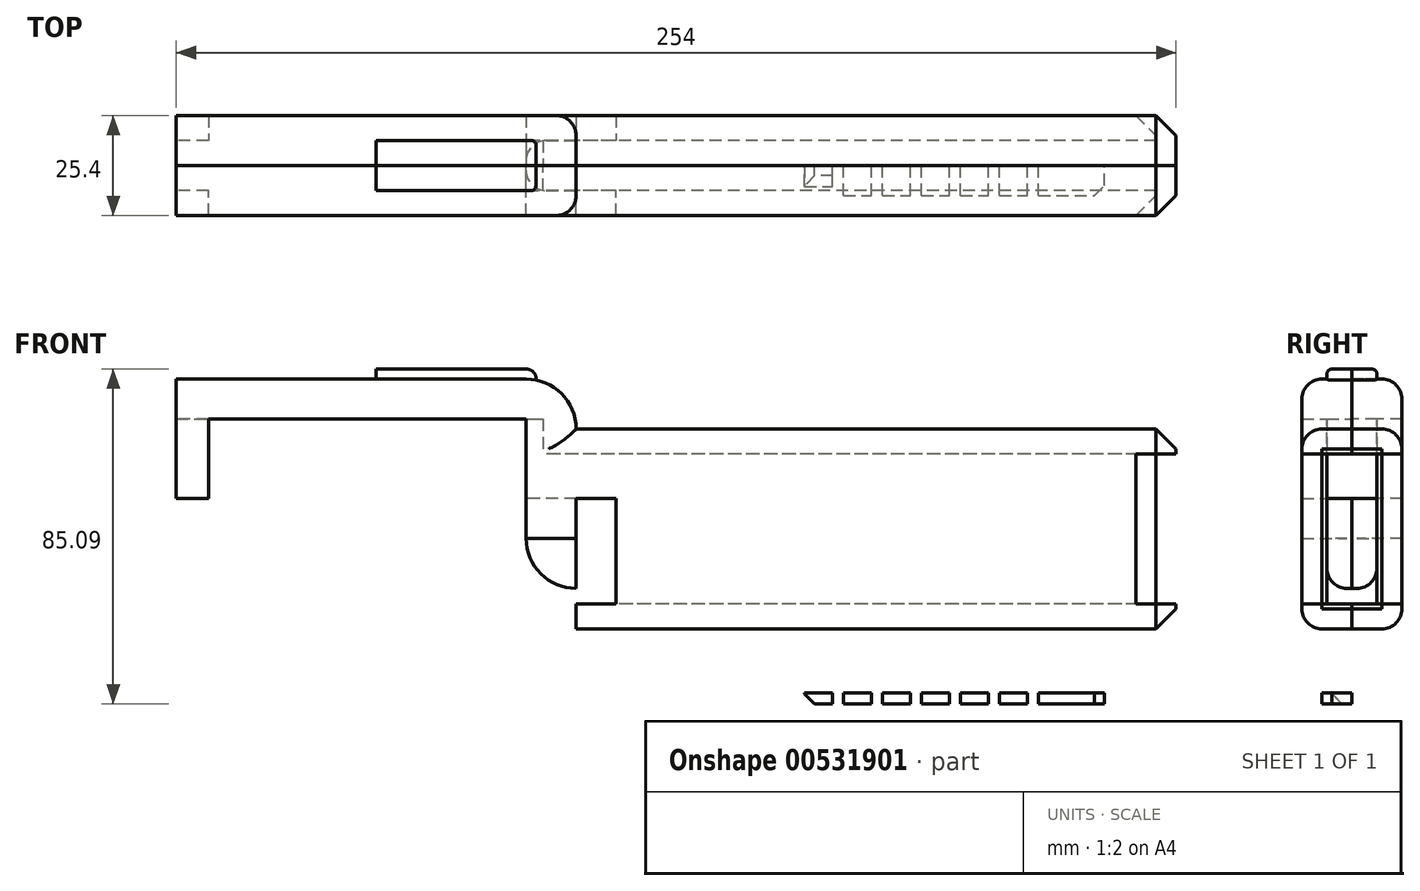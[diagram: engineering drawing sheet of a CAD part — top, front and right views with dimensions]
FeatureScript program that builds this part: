
annotation { "Feature Type Name" : "Feature", "Feature Type Description" : "" }
export const myFeature = defineFeature(function(context is Context, id is Id, definition is map)
    precondition{}
    {
        {
            var Q0;
            Q0=qCreatedBy(makeId("Front.planeOp"),FACE);
            var sketch = newSketch(context, id + "F0", { "sketchPlane" : qUnion([Q0])});
            skLineSegment(sketch, "E0.bottom", {"start": v(-50.8, 20.24) * mm, "end": v(38.1, 20.24) * mm});
            skLineSegment(sketch, "E0.top", {"start": v(-50.8, -20.24) * mm, "end": v(50.8, -20.24) * mm});
            skLineSegment(sketch, "E0.left", {"start": v(-50.8, 20.24) * mm, "end": v(-50.8, -20.24) * mm});
            skLineSegment(sketch, "E0.right", {"start": v(50.8, 7.54) * mm, "end": v(50.8, -20.24) * mm});
            skPoint(sketch, "E0.middle", {"position": v(0, 0) * mm});
            skPoint(sketch, "E1.visualSharp", {"position": v(50.8, 20.24) * mm});
            skArc(sketch, "E1.filletArc", {"start": v(50.8, 7.54) * mm, "mid": v(47.08, 16.52) * mm, "end": v(38.1, 20.24) * mm});
            skPoint(sketch, "E2", {"position": v(0, 20.24) * mm});
            skLineSegment(sketch, "E3", {"start": v(0, 20.24) * mm, "end": v(0, 22.78) * mm});
            skLineSegment(sketch, "E4", {"start": v(0, 22.78) * mm, "end": v(38.1, 22.78) * mm});
            skLineSegment(sketch, "E5", {"start": v(38.1, 22.78) * mm, "end": v(38.1, 20.24) * mm});
            skArc(sketch, "E6", {"start": v(38.1, 22.78) * mm, "mid": v(39.98, 21.95) * mm, "end": v(40.63, 19.99) * mm});
            skLineSegment(sketch, "E7.bottom", {"start": v(50.8, 7.54) * mm, "end": v(203.2, 7.54) * mm});
            skLineSegment(sketch, "E7.top", {"start": v(50.8, -43.26) * mm, "end": v(203.2, -43.26) * mm});
            skLineSegment(sketch, "E7.left", {"start": v(50.8, 7.54) * mm, "end": v(50.8, -43.26) * mm});
            skLineSegment(sketch, "E7.right", {"start": v(203.2, 7.54) * mm, "end": v(203.2, -43.26) * mm});
            skLineSegment(sketch, "E8", {"start": v(38.1, 20.24) * mm, "end": v(38.1, -20.24) * mm});
            skArc(sketch, "E9", {"start": v(38.1, -20.24) * mm, "mid": v(41.82, -29.22) * mm, "end": v(50.8, -32.94) * mm});
            skLineSegment(sketch, "E10.bottom", {"start": v(203.2, 1.2) * mm, "end": v(198.12, 1.2) * mm});
            skLineSegment(sketch, "E10.top", {"start": v(203.2, -36.9) * mm, "end": v(198.12, -36.9) * mm});
            skLineSegment(sketch, "E10.left", {"start": v(203.2, 1.2) * mm, "end": v(203.2, -36.9) * mm});
            skLineSegment(sketch, "E10.right", {"start": v(198.12, 1.2) * mm, "end": v(198.12, -36.9) * mm});
            skLineSegment(sketch, "E11", {"start": v(198.12, 1.2) * mm, "end": v(50.8, 1.2) * mm});
            skLineSegment(sketch, "E12", {"start": v(198.12, -36.9) * mm, "end": v(50.8, -36.9) * mm});
            skLineSegment(sketch, "E13", {"start": v(60.96, 1.2) * mm, "end": v(60.96, -36.9) * mm});
            skLineSegment(sketch, "E14", {"start": v(60.96, -10.08) * mm, "end": v(-42.63, -10.08) * mm});
            skLineSegment(sketch, "E15", {"start": v(-42.63, -10.08) * mm, "end": v(-42.63, 10.08) * mm});
            skLineSegment(sketch, "E16", {"start": v(-42.63, 10.08) * mm, "end": v(42.45, 10.08) * mm});
            skLineSegment(sketch, "E17", {"start": v(42.45, 10.08) * mm, "end": v(42.45, 1.2) * mm});
            skLineSegment(sketch, "E18", {"start": v(42.45, 1.2) * mm, "end": v(50.8, 1.2) * mm});
            skLineSegment(sketch, "E19.bottom", {"start": v(-42.63, 10.08) * mm, "end": v(-50.8, 10.08) * mm});
            skLineSegment(sketch, "E19.top", {"start": v(-42.63, -10.08) * mm, "end": v(-50.8, -10.08) * mm});
            skLineSegment(sketch, "E19.left", {"start": v(-42.63, 10.08) * mm, "end": v(-42.63, -10.08) * mm});
            skLineSegment(sketch, "E19.right", {"start": v(-50.8, 10.08) * mm, "end": v(-50.8, -10.08) * mm});
            skLineSegment(sketch, "E20.bottom", {"start": v(108.84, -43.26) * mm, "end": v(185.04, -43.26) * mm});
            skLineSegment(sketch, "E20.top", {"start": v(108.84, -62.3) * mm, "end": v(185.04, -62.3) * mm});
            skLineSegment(sketch, "E20.left", {"start": v(108.84, -43.26) * mm, "end": v(108.84, -62.3) * mm});
            skLineSegment(sketch, "E20.right", {"start": v(185.04, -43.26) * mm, "end": v(185.04, -62.3) * mm});
            skLineSegment(sketch, "E21", {"start": v(108.84, -59.55) * mm, "end": v(185.04, -59.55) * mm});
            skLineSegment(sketch, "E22", {"start": v(115.95, -59.55) * mm, "end": v(115.95, -62.3) * mm});
            skLineSegment(sketch, "E23", {"start": v(118.74, -59.55) * mm, "end": v(118.74, -62.3) * mm});
            skLineSegment(sketch, "E24", {"start": v(125.85, -59.55) * mm, "end": v(125.85, -62.3) * mm});
            skLineSegment(sketch, "E25", {"start": v(128.65, -59.55) * mm, "end": v(128.65, -62.3) * mm});
            skLineSegment(sketch, "E26", {"start": v(135.76, -59.55) * mm, "end": v(135.76, -62.3) * mm});
            skLineSegment(sketch, "E27", {"start": v(138.55, -59.55) * mm, "end": v(138.55, -62.3) * mm});
            skLineSegment(sketch, "E28", {"start": v(145.67, -59.55) * mm, "end": v(145.67, -62.3) * mm});
            skLineSegment(sketch, "E29", {"start": v(148.46, -59.55) * mm, "end": v(148.46, -62.3) * mm});
            skLineSegment(sketch, "E30", {"start": v(155.57, -59.55) * mm, "end": v(155.57, -62.3) * mm});
            skLineSegment(sketch, "E31", {"start": v(158.37, -59.55) * mm, "end": v(158.37, -62.3) * mm});
            skLineSegment(sketch, "E32", {"start": v(165.48, -59.55) * mm, "end": v(165.48, -62.3) * mm});
            skLineSegment(sketch, "E33", {"start": v(168.27, -59.55) * mm, "end": v(168.27, -62.3) * mm});
            skSolve(sketch);
        }
        {
            var Q0;
            {var subQ0=sQuery(id+"F0.wireOp",EDGE,"E0.left");Q0=makeQuery(id+"F0.imprint","IMPRINT",FACE,{"disambiguationData":[TD([[makeQuery(id+"F0.imprint","IMPRINT",EDGE,{"derivedFrom":subQ0}),1.0]])]});}
            var Q1;
            {var subQ0=sQuery(id+"F0.wireOp",EDGE,"E8");Q1=makeQuery(id+"F0.imprint","IMPRINT",FACE,{"disambiguationData":[TD([[makeQuery(id+"F0.imprint","IMPRINT",EDGE,{"derivedFrom":subQ0}),1.0]])]});}
            var Q2;
            {var subQ3=sQuery(id+"F0.wireOp",EDGE,"E7.bottom");Q2=makeQuery(id+"F0.imprint","IMPRINT",FACE,{"disambiguationData":[TD([[makeQuery(id+"F0.imprint","IMPRINT",EDGE,{"derivedFrom":subQ3}),-1.0]])]});}
            var Q3;
            {var subQ8=sQuery(id+"F0.wireOp",EDGE,"E19.bottom");Q3=makeQuery(id+"F0.imprint","IMPRINT",FACE,{"disambiguationData":[TD([[makeQuery(id+"F0.imprint","IMPRINT",EDGE,{"derivedFrom":subQ8}),-1.0]])]});}
            var Q4;
            {var subQ9=sQuery(id+"F0.wireOp",EDGE,"E17");Q4=makeQuery(id+"F0.imprint","IMPRINT",FACE,{"disambiguationData":[TD([[makeQuery(id+"F0.imprint","IMPRINT",EDGE,{"derivedFrom":subQ9}),1.0]])]});}
            var Q5;
            Q5=makeQuery(id+"F0.imprint","IMPRINT",FACE,{"disambiguationData":[TD([[makeQuery(id+"F0.imprint","IMPRINT",EDGE,{"derivedFrom":sQuery(id+"F0.wireOp",EDGE,"E19.bottom")}),1.0]])]});
            var Q6;
            {var subQ5=sQuery(id+"F0.wireOp",EDGE,"E19.left");Q6=makeQuery(id+"F0.imprint","IMPRINT",FACE,{"disambiguationData":[TD([[makeQuery(id+"F0.imprint","IMPRINT",EDGE,{"derivedFrom":subQ5}),1.0]])]});}
            var Q7;
            {var subQ8=sQuery(id+"F0.wireOp",EDGE,"E17");Q7=makeQuery(id+"F0.imprint","IMPRINT",FACE,{"disambiguationData":[TD([[makeQuery(id+"F0.imprint","IMPRINT",EDGE,{"derivedFrom":subQ8}),-1.0]])]});}
            var Q8;
            {var subQ0=sQuery(id+"F0.wireOp",EDGE,"E11");var subQ5=sQuery(id+"F0.wireOp",EDGE,"E13");var subQ6=makeQuery(id+"F0.imprint","INTERSECT",VERTEX,{"derivedFrom":[subQ0,subQ5]});Q8=makeQuery(id+"F0.imprint","IMPRINT",FACE,{"disambiguationData":[TD([[makeQuery(id+"F0.imprint","IMPRINT",EDGE,{"disambiguationData":[TD([[subQ6,-1.0]])],"derivedFrom":subQ5}),-1.0]])]});}
            var Q9;
            {var subQ1=sQuery(id+"F0.wireOp",EDGE,"E7.left");var subQ6=makeQuery(id+"F0.imprint","INTERSECT",VERTEX,{"derivedFrom":[sQuery(id+"F0.wireOp",EDGE,"E0.top"),subQ1]});Q9=makeQuery(id+"F0.imprint","IMPRINT",FACE,{"disambiguationData":[TD([[makeQuery(id+"F0.imprint","IMPRINT",EDGE,{"disambiguationData":[TD([[subQ6,1.0]])],"derivedFrom":subQ1}),1.0]])]});}
            var Q10;
            {var subQ1=sQuery(id+"F0.wireOp",EDGE,"E10.right");Q10=makeQuery(id+"F0.imprint","IMPRINT",FACE,{"disambiguationData":[TD([[makeQuery(id+"F0.imprint","IMPRINT",EDGE,{"derivedFrom":subQ1}),-1.0]])]});}
            var Q11;
            {var subQ2=sQuery(id+"F0.wireOp",EDGE,"E7.top");Q11=makeQuery(id+"F0.imprint","IMPRINT",FACE,{"disambiguationData":[TD([[makeQuery(id+"F0.imprint","IMPRINT",EDGE,{"derivedFrom":subQ2}),1.0]])]});}
            extrude(context, id + "F1", {"entities" : qUnion([Q0, Q1, Q2, Q3, Q4, Q5, Q6, Q7, Q8, Q9, Q10, Q11]), "depth" : 12.7 * mm, "offsetDistance" : 25.4 * mm});
        }
        {
            var Q0;
            {var subQ2=sQuery(id+"F0.wireOp",EDGE,"E3");Q0=makeQuery(id+"F0.imprint","IMPRINT",FACE,{"disambiguationData":[TD([[makeQuery(id+"F0.imprint","IMPRINT",EDGE,{"derivedFrom":subQ2}),-1.0]])]});}
            var Q1;
            {var subQ0=sQuery(id+"F0.wireOp",EDGE,"E5");Q1=makeQuery(id+"F0.imprint","IMPRINT",FACE,{"disambiguationData":[TD([[makeQuery(id+"F0.imprint","IMPRINT",EDGE,{"derivedFrom":subQ0}),1.0]])]});}
            var Q2;
            {var subQ3=sQuery(id+"F0.wireOp",EDGE,"E9");Q2=makeQuery(id+"F0.imprint","IMPRINT",FACE,{"disambiguationData":[TD([[makeQuery(id+"F0.imprint","IMPRINT",EDGE,{"derivedFrom":subQ3}),1.0]])]});}
            extrude(context, id + "F2", {"entities" : qUnion([Q0, Q1, Q2]), "operationType" : NewBodyOperationType.ADD, "depth" : 6.35 * mm, "offsetDistance" : 25.4 * mm});
        }
        {
            var Q0;
            Q0=makeQuery(id+"F1.opExtrude","CAP_EDGE",EDGE,{"disambiguationData":[OSD([sQuery(id+"F0.wireOp",EDGE,"E0.bottom")])],"isStart":false});
            var Q1;
            Q1=makeQuery(id+"F1.opExtrude","CAP_EDGE",EDGE,{"disambiguationData":[OSD([sQuery(id+"F0.wireOp",EDGE,"E7.bottom")])],"isStart":false});
            var Q2;
            Q2=makeQuery(id+"F2.opExtrude","CAP_EDGE",EDGE,{"disambiguationData":[OSD([sQuery(id+"F0.wireOp",EDGE,"E9")])],"isStart":false});
            var Q3;
            Q3=makeQuery(id+"F1.opExtrude","CAP_EDGE",EDGE,{"disambiguationData":[OSD([sQuery(id+"F0.wireOp",EDGE,"E7.top")])],"isStart":false});
            fillet(context, id + "F3", {"entities" : qUnion([Q0, Q1, Q2, Q3]), "radius" : 5.08 * mm, "tangentPropagation" : true, "allowEdgeOverflow" : false});
        }
        {
            var Q0;
            Q0=makeQuery(id+"F1.opExtrude","CAP_EDGE",EDGE,{"disambiguationData":[OSD([sQuery(id+"F0.wireOp",EDGE,"E7.right")])],"isStart":false});
            var Q1;
            Q1=makeQuery(id+"F1.opExtrude","CAP_EDGE",EDGE,{"disambiguationData":[OSD([sQuery(id+"F0.wireOp",EDGE,"E10.right")])],"isStart":false});
            chamfer(context, id + "F4", {"entities" : qUnion([Q0, Q1]), "width" : 5.08 * mm, "tangentPropagation" : true});
        }
        {
            var Q0;
            Q0=makeQuery(id+"F2.opExtrude","CAP_EDGE",EDGE,{"disambiguationData":[OSD([sQuery(id+"F0.wireOp",EDGE,"E4")])],"isStart":false});
            fillet(context, id + "F5", {"entities" : qUnion([Q0]), "radius" : 1.27 * mm, "tangentPropagation" : true, "allowEdgeOverflow" : false});
        }
        {
            var Q0;
            {var subQ1=sQuery(id+"F0.wireOp",EDGE,"E10.right");Q0=makeQuery(id+"F0.imprint","IMPRINT",FACE,{"disambiguationData":[TD([[makeQuery(id+"F0.imprint","IMPRINT",EDGE,{"derivedFrom":subQ1}),-1.0]])]});}
            var Q1;
            {var subQ0=sQuery(id+"F0.wireOp",EDGE,"E11");var subQ5=sQuery(id+"F0.wireOp",EDGE,"E13");var subQ6=makeQuery(id+"F0.imprint","INTERSECT",VERTEX,{"derivedFrom":[subQ0,subQ5]});Q1=makeQuery(id+"F0.imprint","IMPRINT",FACE,{"disambiguationData":[TD([[makeQuery(id+"F0.imprint","IMPRINT",EDGE,{"disambiguationData":[TD([[subQ6,-1.0]])],"derivedFrom":subQ5}),-1.0]])]});}
            var Q2;
            {var subQ5=sQuery(id+"F0.wireOp",EDGE,"E19.left");Q2=makeQuery(id+"F0.imprint","IMPRINT",FACE,{"disambiguationData":[TD([[makeQuery(id+"F0.imprint","IMPRINT",EDGE,{"derivedFrom":subQ5}),1.0]])]});}
            var Q3;
            Q3=makeQuery(id+"F0.imprint","IMPRINT",FACE,{"disambiguationData":[TD([[makeQuery(id+"F0.imprint","IMPRINT",EDGE,{"derivedFrom":sQuery(id+"F0.wireOp",EDGE,"E19.bottom")}),1.0]])]});
            var Q4;
            {var subQ8=sQuery(id+"F0.wireOp",EDGE,"E17");Q4=makeQuery(id+"F0.imprint","IMPRINT",FACE,{"disambiguationData":[TD([[makeQuery(id+"F0.imprint","IMPRINT",EDGE,{"derivedFrom":subQ8}),-1.0]])]});}
            extrude(context, id + "F6", {"entities" : qUnion([Q0, Q1, Q2, Q3, Q4]), "operationType" : NewBodyOperationType.REMOVE, "depth" : 6.35 * mm, "offsetDistance" : 25.4 * mm});
        }
        {
            var Q0;
            {var subQ4=sQuery(id+"F0.wireOp",EDGE,"E20.bottom");Q0=makeQuery(id+"F0.imprint","IMPRINT",FACE,{"disambiguationData":[TD([[makeQuery(id+"F0.imprint","IMPRINT",EDGE,{"derivedFrom":subQ4}),-1.0]])]});}
            var Q1;
            {var subQ3=sQuery(id+"F0.wireOp",EDGE,"E22");Q1=makeQuery(id+"F0.imprint","IMPRINT",FACE,{"disambiguationData":[TD([[makeQuery(id+"F0.imprint","IMPRINT",EDGE,{"derivedFrom":subQ3}),-1.0]])]});}
            var Q2;
            {var subQ0=sQuery(id+"F0.wireOp",EDGE,"E23");Q2=makeQuery(id+"F0.imprint","IMPRINT",FACE,{"disambiguationData":[TD([[makeQuery(id+"F0.imprint","IMPRINT",EDGE,{"derivedFrom":subQ0}),1.0]])]});}
            var Q3;
            {var subQ0=sQuery(id+"F0.wireOp",EDGE,"E25");Q3=makeQuery(id+"F0.imprint","IMPRINT",FACE,{"disambiguationData":[TD([[makeQuery(id+"F0.imprint","IMPRINT",EDGE,{"derivedFrom":subQ0}),1.0]])]});}
            var Q4;
            {var subQ0=sQuery(id+"F0.wireOp",EDGE,"E27");Q4=makeQuery(id+"F0.imprint","IMPRINT",FACE,{"disambiguationData":[TD([[makeQuery(id+"F0.imprint","IMPRINT",EDGE,{"derivedFrom":subQ0}),1.0]])]});}
            var Q5;
            {var subQ0=sQuery(id+"F0.wireOp",EDGE,"E29");Q5=makeQuery(id+"F0.imprint","IMPRINT",FACE,{"disambiguationData":[TD([[makeQuery(id+"F0.imprint","IMPRINT",EDGE,{"derivedFrom":subQ0}),1.0]])]});}
            var Q6;
            {var subQ0=sQuery(id+"F0.wireOp",EDGE,"E31");Q6=makeQuery(id+"F0.imprint","IMPRINT",FACE,{"disambiguationData":[TD([[makeQuery(id+"F0.imprint","IMPRINT",EDGE,{"derivedFrom":subQ0}),1.0]])]});}
            var Q7;
            {var subQ3=sQuery(id+"F0.wireOp",EDGE,"E33");Q7=makeQuery(id+"F0.imprint","IMPRINT",FACE,{"disambiguationData":[TD([[makeQuery(id+"F0.imprint","IMPRINT",EDGE,{"derivedFrom":subQ3}),1.0]])]});}
            extrude(context, id + "F7", {"entities" : qUnion([Q0, Q1, Q2, Q3, Q4, Q5, Q6, Q7]), "operationType" : NewBodyOperationType.ADD, "depth" : 7.62 * mm, "offsetDistance" : 25.4 * mm});
        }
        {
            var Q0;
            Q0=makeQuery(id+"F1.opExtrude","SWEPT_BODY",BODY,{"disambiguationData":[OSD([sQuery(id+"F0.wireOp",EDGE,"E0.bottom"),sQuery(id+"F0.wireOp",EDGE,"E0.top"),sQuery(id+"F0.wireOp",EDGE,"E0.left"),sQuery(id+"F0.wireOp",EDGE,"E1.filletArc"),sQuery(id+"F0.wireOp",EDGE,"E7.bottom"),sQuery(id+"F0.wireOp",EDGE,"E7.top"),sQuery(id+"F0.wireOp",EDGE,"E7.left"),sQuery(id+"F0.wireOp",EDGE,"E7.right"),sQuery(id+"F0.wireOp",EDGE,"E10.bottom"),sQuery(id+"F0.wireOp",EDGE,"E10.top"),sQuery(id+"F0.wireOp",EDGE,"E10.right"),sQuery(id+"F0.wireOp",EDGE,"E19.right")])]});
            var Q1;
            Q1=qCreatedBy(makeId("Front.planeOp"),FACE);
            mirror(context, id + "F8", {"operationType" : NewBodyOperationType.ADD, "entities" : qUnion([Q0]), "mirrorPlane" : qUnion([Q1])});
        }
        {
            var Q0;
            Q0=qCreatedBy(makeId("Top.planeOp"),FACE);
            var sketch = newSketch(context, id + "F9", { "sketchPlane" : qUnion([Q0])});
            skLineSegment(sketch, "E34", {"start": v(0, 0) * mm, "end": v(-25.4, 0) * mm});
            skLineSegment(sketch, "E35.bottom", {"start": v(-50.8, -6.35) * mm, "end": v(0, -6.35) * mm});
            skLineSegment(sketch, "E35.top", {"start": v(-50.8, 6.35) * mm, "end": v(0, 6.35) * mm});
            skLineSegment(sketch, "E35.left", {"start": v(-50.8, -6.35) * mm, "end": v(-50.8, 6.35) * mm});
            skLineSegment(sketch, "E35.right", {"start": v(0, -6.35) * mm, "end": v(0, 6.35) * mm});
            skPoint(sketch, "E35.middle", {"position": v(-25.4, 0) * mm});
            skSolve(sketch);
        }
        {
            var Q0;
            Q0 = qSketchRegion(id + "F9", true);
            extrude(context, id + "F10", {"entities" : qUnion([Q0]), "operationType" : NewBodyOperationType.REMOVE, "oppositeDirection" : true, "depth" : 79.76 * mm, "offsetDistance" : 25.4 * mm});
        }
        {
            var Q0;
            {var subQ0=sQuery(id+"F0.wireOp",EDGE,"E20.top");Q0=makeQuery(id+"F7.opExtrude","CAP_EDGE",EDGE,{"disambiguationData":[OSD([subQ0]),TDD([makeQuery(id+"F0.imprint","IMPRINT",EDGE,{"disambiguationData":[TD([[makeQuery(id+"F0.imprint","INTERSECT",VERTEX,{"derivedFrom":[subQ0,sQuery(id+"F0.wireOp",EDGE,"E20.left")]}),-1.0]])],"derivedFrom":subQ0})])],"isStart":false});}
            var Q1;
            {var subQ0=sQuery(id+"F0.wireOp",EDGE,"E20.top");Q1=makeQuery(id+"F8.opPattern","COPY",EDGE,{"derivedFrom":makeQuery(id+"F7.opExtrude","CAP_EDGE",EDGE,{"disambiguationData":[OSD([subQ0]),TDD([makeQuery(id+"F0.imprint","IMPRINT",EDGE,{"disambiguationData":[TD([[makeQuery(id+"F0.imprint","INTERSECT",VERTEX,{"derivedFrom":[subQ0,sQuery(id+"F0.wireOp",EDGE,"E23")]}),-1.0]])],"derivedFrom":subQ0})])],"isStart":false}),"instanceName":"1"});}
            chamfer(context, id + "F11", {"entities" : qUnion([Q0, Q1]), "width" : 5.08 * mm, "tangentPropagation" : true});
        }
        {
            var Q0;
            Q0=makeQuery(id+"F7.opExtrude","CAP_EDGE",EDGE,{"disambiguationData":[OSD([sQuery(id+"F0.wireOp",EDGE,"E20.right")])],"isStart":false});
            var Q1;
            Q1=makeQuery(id+"F8.opPattern","COPY",EDGE,{"derivedFrom":makeQuery(id+"F7.opExtrude","CAP_EDGE",EDGE,{"disambiguationData":[OSD([sQuery(id+"F0.wireOp",EDGE,"E20.right")])],"isStart":false}),"instanceName":"1"});
            var Q2;
            {var subQ0=makeQuery(id+"F7.opExtrude","SWEPT_EDGE",EDGE,{"disambiguationData":[OSD([sQuery(id+"F0.wireOp",EDGE,"E20.top"),sQuery(id+"F0.wireOp",EDGE,"E20.left")])]});Q2=makeQuery(id+"F8.boolean.opBoolean","MERGE",EDGE,{"derivedFrom":[subQ0,makeQuery(id+"F8.opPattern","COPY",EDGE,{"derivedFrom":subQ0,"instanceName":"1"})]});}
            chamfer(context, id + "F12", {"entities" : qUnion([Q0, Q1, Q2]), "width" : 2.54 * mm, "tangentPropagation" : true});
        }
    });
